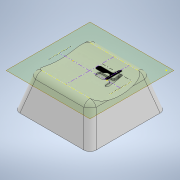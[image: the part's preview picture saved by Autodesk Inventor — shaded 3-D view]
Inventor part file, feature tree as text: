
AUTODESK INVENTOR PART (.ipt)
format: ipt  version: 2022 (Build 260153000, 153)  size: 257,024 bytes
history: native  units: in
note: dims shown in document units (in); Inventor stores cm internally (conversion verified against a paired STEP export)
features: extrude x6, sketch x6, plane x2, fillet x1
ambient origin geometry x8: Origin, YZ Plane, XZ Plane, XY Plane, X Axis, Y Axis, Z Axis, Center Point
bodies: Solid1 (feature_tree)
feature tree (15):
  extrude  "Extrusion1"  Depth=0.7087in
  fillet  "Fillet1"  Radius=0.315in
  plane  "Work Plane1"
  extrude  "Extrusion2"  Depth=0.4724in
  extrude  "Extrusion3"  Depth=0.6299in
  extrude  "Extrusion4"  Depth=0.1772in
  extrude  "Extrusion5"  Depth=0.1575in TaperAngle=0.0deg
  plane  "Work Plane2"
  sketch  "Sketch6"  dims[d15=0.0472in d16=0.1634in d17=0.1634in d18=0.0472in d19=0.0118in d20=0.1575in d21=0.0in d22=0.063in d23=0.0in]
  extrude  "Extrusion6"  Depth=0.1634in
  sketch  "Sketch1"  dims[d0=0.7087in d1=0.7087in d2=0.315in d3=-0.1031in]
  sketch  "Sketch2"  dims[d4=0.0591in d5=0.4724in]
  sketch  "Sketch3"  dims[d6=0.0in d7=0.0in d8=0.6299in]
  sketch  "Sketch4"  dims[d9=0.6299in d10=0.1772in d11=-0.1031in]
  sketch  "Sketch5"  dims[d12=0.2185in d13=0.1575in d14=0.0in]
